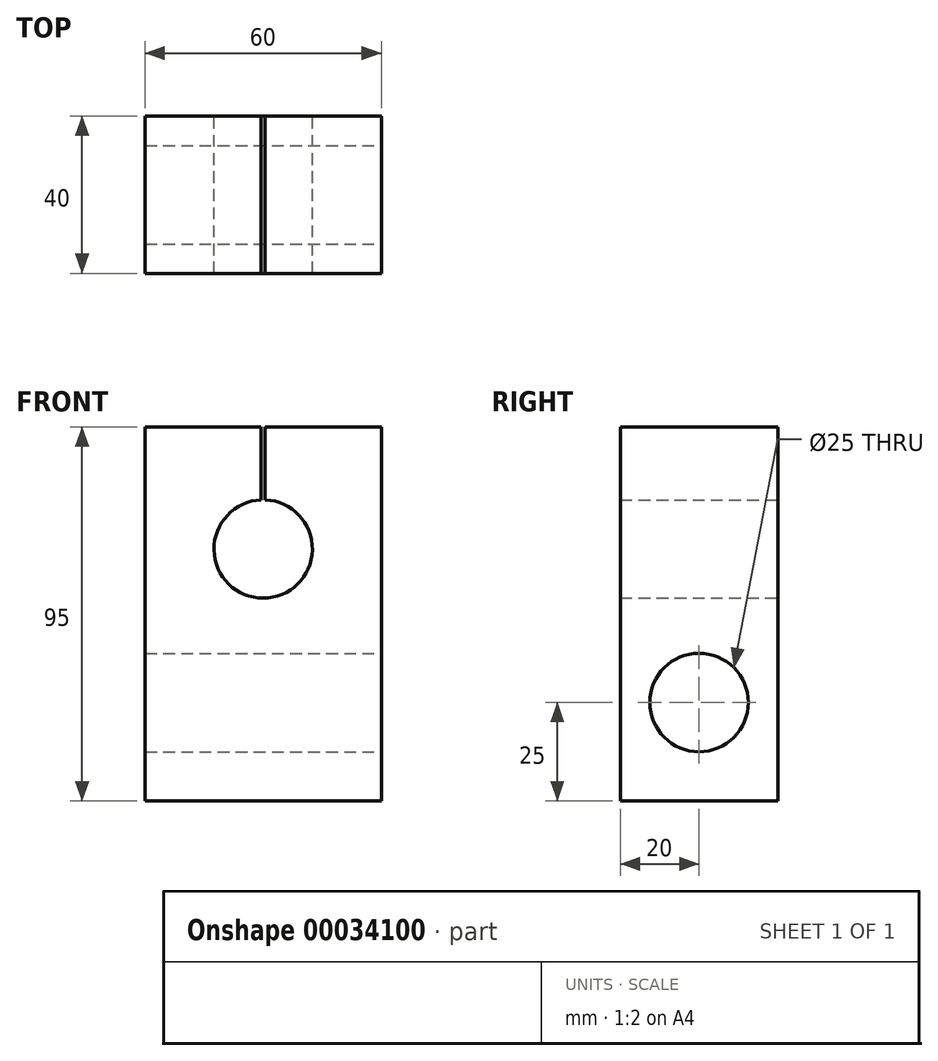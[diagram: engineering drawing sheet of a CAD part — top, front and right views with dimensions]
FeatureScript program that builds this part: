
annotation { "Feature Type Name" : "Feature", "Feature Type Description" : "" }
export const myFeature = defineFeature(function(context is Context, id is Id, definition is map)
    precondition{}
    {
        {
            var Q0;
            Q0=qCreatedBy(makeId("Front.planeOp"),FACE);
            var sketch = newSketch(context, id + "F0", { "sketchPlane" : qUnion([Q0])});
            skLineSegment(sketch, "E0.bottom", {"start": v(-30, 0) * mm, "end": v(30, 0) * mm});
            skLineSegment(sketch, "E0.top", {"start": v(-30, 95) * mm, "end": v(-0.5, 95) * mm});
            skLineSegment(sketch, "E0.left", {"start": v(-30, 0) * mm, "end": v(-30, 95) * mm});
            skLineSegment(sketch, "E0.right", {"start": v(30, 0) * mm, "end": v(30, 95) * mm});
            skArc(sketch, "E1", {"start": v(-0.5, 76.49) * mm, "mid": v(0, 51.5) * mm, "end": v(0.5, 76.49) * mm});
            skLineSegment(sketch, "E2", {"start": v(-0.5, 95) * mm, "end": v(-0.5, 76.49) * mm});
            skLineSegment(sketch, "E3.MirrorCS", {"start": v(0.5, 95) * mm, "end": v(0.5, 76.49) * mm});
            skLineSegment(sketch, "E4.trimOffspring", {"start": v(0.5, 95) * mm, "end": v(30, 95) * mm});
            skSolve(sketch);
        }
        {
            var Q0;
            Q0 = qSketchRegion(id + "F0", true);
            extrude(context, id + "F1", {"entities" : qUnion([Q0]), "depth" : 40 * mm});
        }
        {
            var Q0;
            Q0=makeQuery(id+"F1.opExtrude","SWEPT_FACE",FACE,{"disambiguationData":[OSD([sQuery(id+"F0.wireOp",EDGE,"E0.right")])]});
            var sketch = newSketch(context, id + "F2", { "sketchPlane" : qUnion([Q0])});
            skPoint(sketch, "E5", {"position": v(-20, 25) * mm});
            skCircle(sketch, "E6", {"center": v(-20, 25) * mm, "radius": 12.5 * mm});
            skSolve(sketch);
        }
        {
            var Q0;
            Q0=makeQuery(id+"F2.imprint","IMPRINT",FACE,{"disambiguationData":[TD([[makeQuery(id+"F2.imprint","IMPRINT",EDGE,{"derivedFrom":sQuery(id+"F2.wireOp",EDGE,"E6")}),1.0]])]});
            extrude(context, id + "F3", {"entities" : qUnion([Q0]), "operationType" : NewBodyOperationType.REMOVE, "endBound" : BoundingType.THROUGH_ALL, "oppositeDirection" : true, "depth" : 25 * mm});
        }
    });
